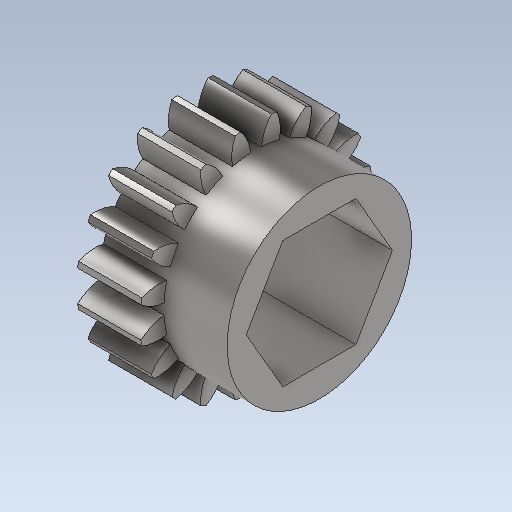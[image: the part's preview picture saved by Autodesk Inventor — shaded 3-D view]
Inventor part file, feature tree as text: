
AUTODESK INVENTOR PART (.ipt)
format: ipt  version: 2023 (Build 270158000, 158)  size: 338,944 bytes
history: native  units: in
note: dims shown in document units (in); Inventor stores cm internally (conversion verified against a paired STEP export)
features: other x3, sketch x3
ambient origin geometry x8: Origin, YZ Plane, XZ Plane, XY Plane, X Axis, Y Axis, Z Axis, Center Point
bodies: Solid1 (feature_tree)
feature tree (6):
  other  "CH-1-01-20T_Idler.ipt"
  other  "Solid1::CH-1-01-20T_Idler.ipt"
  other  "TaggingFeature1"
  sketch  "Sketch3"  dims[d0=0.3937in]
  sketch  "Sketch5"
  sketch  "Sketch4"
